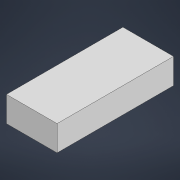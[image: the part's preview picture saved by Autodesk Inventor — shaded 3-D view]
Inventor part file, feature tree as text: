
AUTODESK INVENTOR PART (.ipt)
format: ipt  version: 2021 (Build 250183000, 183)  size: 86,528 bytes
history: native  units: mm
features: extrude x1, sketch x1
ambient origin geometry x8: Origin, YZ Plane, XZ Plane, XY Plane, X Axis, Y Axis, Z Axis, Center Point
bodies: Solid1 (feature_tree)
feature tree (2):
  extrude  "Extrusion1"  Depth=20.0mm
  sketch  "Sketch1"  dims[d0=92.0mm d1=46.0mm d2=40.0mm d3=20.0mm d4=20.0mm d5=0.0mm]
